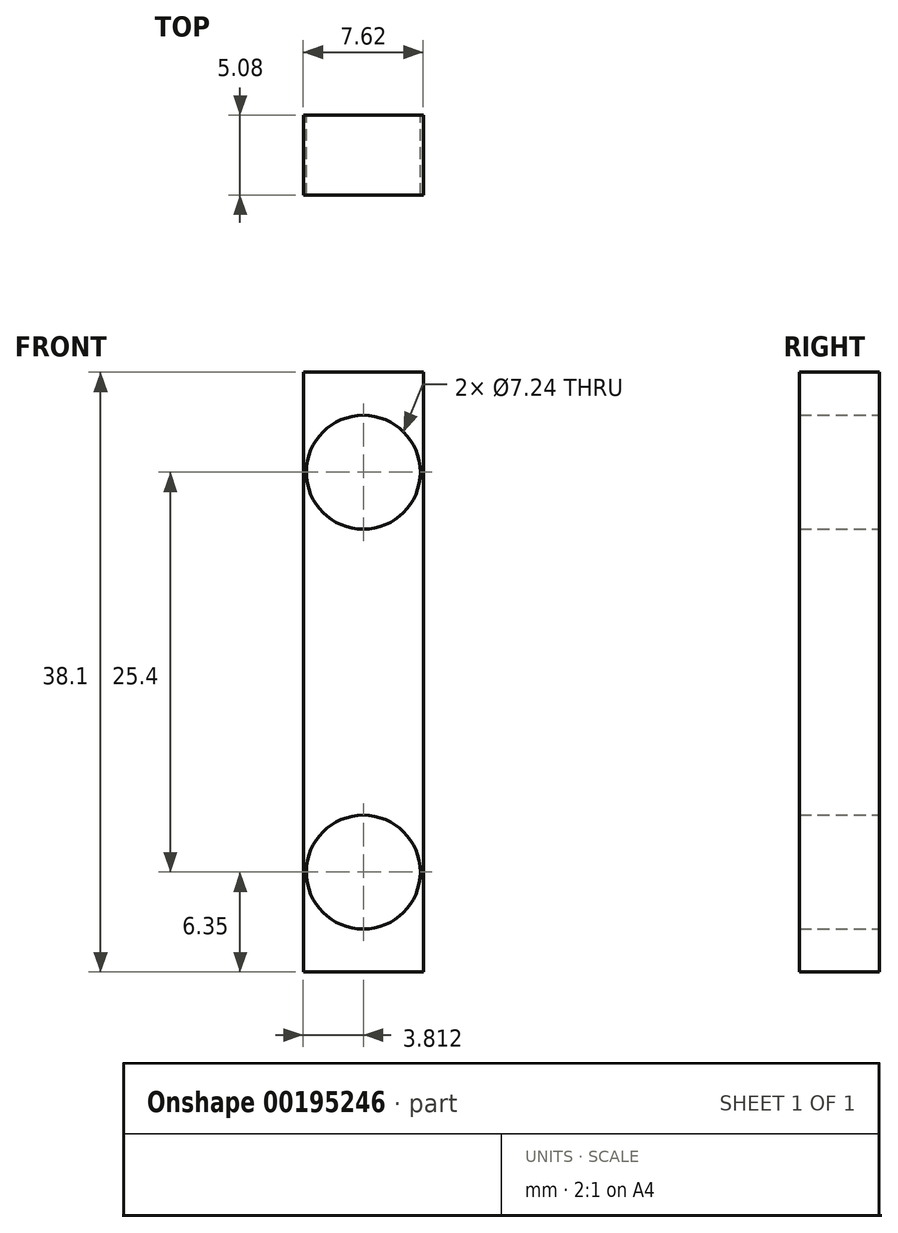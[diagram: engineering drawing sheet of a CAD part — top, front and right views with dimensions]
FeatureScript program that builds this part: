
annotation { "Feature Type Name" : "Feature", "Feature Type Description" : "" }
export const myFeature = defineFeature(function(context is Context, id is Id, definition is map)
    precondition{}
    {
        {
            var Q0;
            Q0=qCreatedBy(makeId("Front.planeOp"),FACE);
            var sketch = newSketch(context, id + "F0", { "sketchPlane" : qUnion([Q0])});
            skLineSegment(sketch, "E0.bottom", {"start": v(-5.54, 20.8) * mm, "end": v(2.08, 20.8) * mm});
            skLineSegment(sketch, "E0.top", {"start": v(-5.54, -17.3) * mm, "end": v(2.08, -17.3) * mm});
            skLineSegment(sketch, "E0.left", {"start": v(-5.54, 20.8) * mm, "end": v(-5.54, -17.3) * mm});
            skLineSegment(sketch, "E0.right", {"start": v(2.08, 20.8) * mm, "end": v(2.08, -17.3) * mm});
            skSolve(sketch);
        }
        {
            var Q0;
            Q0 = qSketchRegion(id + "F0", true);
            extrude(context, id + "F1", {"entities" : qUnion([Q0]), "depth" : 5.08 * mm});
        }
        {
            var Q0;
            Q0=qCreatedBy(makeId("Front.planeOp"),FACE);
            var sketch = newSketch(context, id + "F2", { "sketchPlane" : qUnion([Q0])});
            skCircle(sketch, "E1", {"center": v(-1.73, 14.45) * mm, "radius": 3.62 * mm, "construction": true});
            skCircle(sketch, "E2", {"center": v(-1.73, -10.95) * mm, "radius": 3.62 * mm, "construction": true});
            skSolve(sketch);
        }
        {
            var Q0;
            Q0=sQuery(id+"F2.wireOp",VERTEX,"E1.center");
            var Q1;
            Q1=sQuery(id+"F2.wireOp",VERTEX,"E2.center");
            var Q2;
            Q2=makeQuery(id+"F1.opExtrude","SWEPT_BODY",BODY,{"disambiguationData":[OSD([sQuery(id+"F0.wireOp",EDGE,"E0.bottom"),sQuery(id+"F0.wireOp",EDGE,"E0.top"),sQuery(id+"F0.wireOp",EDGE,"E0.left"),sQuery(id+"F0.wireOp",EDGE,"E0.right")])]});
            hole(context, id + "F3", {"style" : HoleStyle.SIMPLE, "endStyle" : HoleEndStyle.THROUGH, "oppositeDirection" : true, "holeDiameter" : 7.24 * mm, "locations" : qUnion([Q0, Q1]), "scope" : qUnion([Q2]), "isTappedThrough" : true});
        }
    });
